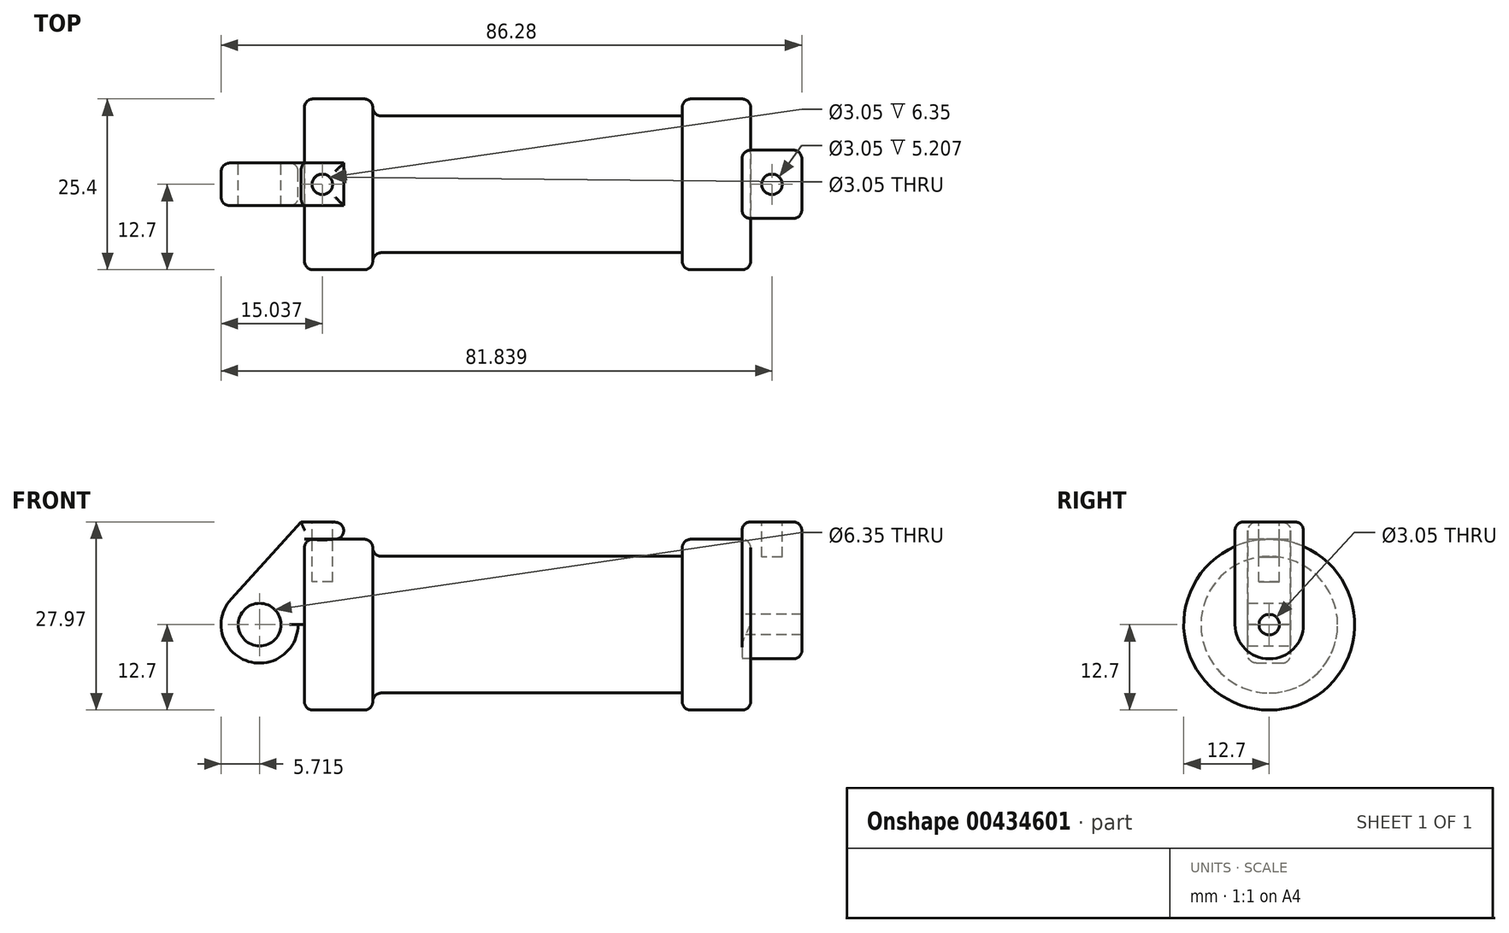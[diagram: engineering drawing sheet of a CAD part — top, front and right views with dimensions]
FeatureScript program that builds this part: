
annotation { "Feature Type Name" : "Feature", "Feature Type Description" : "" }
export const myFeature = defineFeature(function(context is Context, id is Id, definition is map)
    precondition{}
    {
        {
            var Q0;
            Q0=qCreatedBy(makeId("Front.planeOp"),FACE);
            var sketch = newSketch(context, id + "F0", { "sketchPlane" : qUnion([Q0])});
            skLineSegment(sketch, "E0", {"start": v(0, 0) * mm, "end": v(0, 12.7) * mm});
            skLineSegment(sketch, "E1", {"start": v(0, 12.7) * mm, "end": v(10.16, 12.7) * mm});
            skLineSegment(sketch, "E2", {"start": v(10.16, 12.7) * mm, "end": v(10.16, 10.16) * mm});
            skLineSegment(sketch, "E3", {"start": v(10.16, 10.16) * mm, "end": v(56.13, 10.16) * mm});
            skLineSegment(sketch, "E4", {"start": v(56.13, 10.16) * mm, "end": v(56.13, 12.7) * mm});
            skLineSegment(sketch, "E5", {"start": v(56.13, 12.7) * mm, "end": v(66.3, 12.7) * mm});
            skLineSegment(sketch, "E6", {"start": v(66.3, 12.7) * mm, "end": v(66.3, 0) * mm});
            skLineSegment(sketch, "E7", {"start": v(66.3, 0) * mm, "end": v(0, 0) * mm});
            skLineSegment(sketch, "E8", {"start": v(5.84, 15.24) * mm, "end": v(-0.5, 15.24) * mm});
            skLineSegment(sketch, "E9", {"start": v(-0.5, 15.24) * mm, "end": v(-10.88, 3.85) * mm});
            skLineSegment(sketch, "E10", {"start": v(0, 0) * mm, "end": v(-6.65, 0) * mm});
            skCircle(sketch, "E11", {"center": v(-6.65, 0) * mm, "radius": 5.72 * mm});
            skCircle(sketch, "E12", {"center": v(-6.65, 0) * mm, "radius": 3.18 * mm});
            skLineSegment(sketch, "E13", {"start": v(5.84, 15.24) * mm, "end": v(5.84, -9.4) * mm});
            skLineSegment(sketch, "E14", {"start": v(5.84, -9.4) * mm, "end": v(-8.18, -5.5) * mm});
            skSolve(sketch);
        }
        {
            var Q0;
            {var subQ1=sQuery(id+"F0.wireOp",EDGE,"E0");Q0=makeQuery(id+"F0.imprint","IMPRINT",FACE,{"disambiguationData":[TD([[makeQuery(id+"F0.imprint","IMPRINT",EDGE,{"derivedFrom":subQ1}),1.0]])]});}
            var Q1;
            {var subQ5=sQuery(id+"F0.wireOp",EDGE,"E12");Q1=makeQuery(id+"F0.imprint","IMPRINT",FACE,{"disambiguationData":[TD([[makeQuery(id+"F0.imprint","IMPRINT",EDGE,{"derivedFrom":subQ5}),-1.0]])]});}
            extrude(context, id + "F1", {"entities" : qUnion([Q0, Q1]), "endBound" : BoundingType.SYMMETRIC, "depth" : 6.35 * mm});
        }
        {
            var Q0;
            {var subQ0=sQuery(id+"F0.wireOp",EDGE,"E0");Q0=makeQuery(id+"F0.imprint","IMPRINT",FACE,{"disambiguationData":[TD([[makeQuery(id+"F0.imprint","IMPRINT",EDGE,{"derivedFrom":subQ0}),-1.0]])]});}
            var Q1;
            {var subQ0=sQuery(id+"F0.wireOp",EDGE,"E2");Q1=makeQuery(id+"F0.imprint","IMPRINT",FACE,{"disambiguationData":[TD([[makeQuery(id+"F0.imprint","IMPRINT",EDGE,{"derivedFrom":subQ0}),-1.0]])]});}
            var Q2;
            Q2=sQuery(id+"F0.wireOp",EDGE,"E7");
            revolve(context, id + "F2", {"entities" : qUnion([Q0, Q1]), "axis" : qUnion([Q2]), "revolveType" : RevolveType.FULL});
        }
        {
            var Q0;
            Q0=makeQuery(id+"F2.opRevolve","SWEPT_FACE",FACE,{"disambiguationData":[OSD([sQuery(id+"F0.wireOp",EDGE,"E6")])]});
            var sketch = newSketch(context, id + "F3", { "sketchPlane" : qUnion([Q0])});
            skCircle(sketch, "E15", {"center": v(0, 0) * mm, "radius": 1.52 * mm});
            skCircle(sketch, "E16", {"center": v(0, 0) * mm, "radius": 5.08 * mm});
            skLineSegment(sketch, "E17", {"start": v(-5.08, 0) * mm, "end": v(-5.08, 15.27) * mm});
            skLineSegment(sketch, "E18", {"start": v(5.08, 0) * mm, "end": v(5.08, 15.27) * mm});
            skLineSegment(sketch, "E19", {"start": v(5.08, 15.27) * mm, "end": v(-5.08, 15.27) * mm});
            skSolve(sketch);
        }
        {
            var Q0;
            {var subQ0=sQuery(id+"F3.wireOp",EDGE,"E17");var subQ1=sQuery(id+"F3.wireOp",EDGE,"E16");var subQ2=makeQuery(id+"F3.imprint","INTERSECT",VERTEX,{"derivedFrom":[subQ1,subQ0]});Q0=makeQuery(id+"F3.imprint","IMPRINT",FACE,{"disambiguationData":[TD([[makeQuery(id+"F3.imprint","IMPRINT",EDGE,{"disambiguationData":[TD([[subQ2,1.0]])],"derivedFrom":subQ1}),-1.0]])]});}
            var Q1;
            {var subQ0=sQuery(id+"F3.wireOp",EDGE,"E19");Q1=makeQuery(id+"F3.imprint","IMPRINT",FACE,{"disambiguationData":[TD([[makeQuery(id+"F3.imprint","IMPRINT",EDGE,{"derivedFrom":subQ0}),1.0]])]});}
            var Q2;
            Q2=makeQuery(id+"F3.imprint","IMPRINT",FACE,{"disambiguationData":[TD([[makeQuery(id+"F3.imprint","IMPRINT",EDGE,{"derivedFrom":sQuery(id+"F3.wireOp",EDGE,"E15")}),-1.0]])]});
            extrude(context, id + "F4", {"entities" : qUnion([Q0, Q1, Q2]), "depth" : 7.62 * mm, "hasSecondDirection" : true, "secondDirectionOppositeDirection" : true, "secondDirectionDepth" : 1.27 * mm});
        }
        {
            var Q0;
            Q0=makeQuery(id+"F4.opExtrude","SWEPT_FACE",FACE,{"disambiguationData":[OSD([sQuery(id+"F3.wireOp",EDGE,"E19")])]});
            var sketch = newSketch(context, id + "F5", { "sketchPlane" : qUnion([Q0])});
            skCircle(sketch, "E20", {"center": v(69.47, 0) * mm, "radius": 1.52 * mm});
            skPoint(sketch, "E21.orphan", {"position": v(69.47, 5.08) * mm});
            skPoint(sketch, "E22.orphan", {"position": v(73.91, 0) * mm});
            skPoint(sketch, "E23.orphan", {"position": v(69.47, -5.08) * mm});
            skPoint(sketch, "E24.start.orphan", {"position": v(65.02, 0) * mm});
            skSolve(sketch);
        }
        {
            var Q0;
            Q0=makeQuery(id+"F5.imprint","IMPRINT",FACE,{"disambiguationData":[TD([[makeQuery(id+"F5.imprint","IMPRINT",EDGE,{"derivedFrom":sQuery(id+"F5.wireOp",EDGE,"E20")}),1.0]])]});
            extrude(context, id + "F6", {"entities" : qUnion([Q0]), "operationType" : NewBodyOperationType.REMOVE, "endBound" : BoundingType.SYMMETRIC, "oppositeDirection" : true, "depth" : 10.4 * mm});
        }
        {
            var Q0;
            Q0=makeQuery(id+"F1.opExtrude","SWEPT_FACE",FACE,{"disambiguationData":[OSD([sQuery(id+"F0.wireOp",EDGE,"E8")])]});
            var sketch = newSketch(context, id + "F7", { "sketchPlane" : qUnion([Q0])});
            skCircle(sketch, "E25", {"center": v(2.67, 0) * mm, "radius": 1.52 * mm});
            skPoint(sketch, "E26.trimOffspring.end.orphan", {"position": v(5.84, 0) * mm});
            skPoint(sketch, "E27.trimOffspring.end.orphan", {"position": v(2.67, -3.18) * mm});
            skPoint(sketch, "E28.start.orphan", {"position": v(-0.5, 0) * mm});
            skPoint(sketch, "E29.start.orphan", {"position": v(2.67, 3.18) * mm});
            skSolve(sketch);
        }
        {
            var Q0;
            Q0 = qSketchRegion(id + "F7", true);
            extrude(context, id + "F8", {"entities" : qUnion([Q0]), "operationType" : NewBodyOperationType.REMOVE, "endBound" : BoundingType.SYMMETRIC, "oppositeDirection" : true, "depth" : 17.78 * mm});
        }
        {
            var Q0;
            Q0=makeQuery(id+"F1.opExtrude","CAP_EDGE",EDGE,{"disambiguationData":[OSD([sQuery(id+"F0.wireOp",EDGE,"E8")])],"isStart":true});
            var Q1;
            Q1=makeQuery(id+"F1.opExtrude","SWEPT_EDGE",EDGE,{"disambiguationData":[OSD([sQuery(id+"F0.wireOp",EDGE,"E8"),sQuery(id+"F0.wireOp",EDGE,"E13")])]});
            var Q2;
            Q2=makeQuery(id+"F1.opExtrude","CAP_EDGE",EDGE,{"disambiguationData":[OSD([sQuery(id+"F0.wireOp",EDGE,"E8")])],"isStart":false});
            var Q3;
            Q3=makeQuery(id+"F1.opExtrude","CAP_EDGE",EDGE,{"disambiguationData":[OSD([sQuery(id+"F0.wireOp",EDGE,"E9")])],"isStart":false});
            var Q4;
            Q4=makeQuery(id+"F1.opExtrude","CAP_EDGE",EDGE,{"disambiguationData":[OSD([sQuery(id+"F0.wireOp",EDGE,"E11")])],"isStart":false});
            var Q5;
            Q5=makeQuery(id+"F1.opExtrude","SWEPT_EDGE",EDGE,{"disambiguationData":[OSD([sQuery(id+"F0.wireOp",EDGE,"E1"),sQuery(id+"F0.wireOp",EDGE,"E13")])]});
            var Q6;
            Q6=makeQuery(id+"F1.opExtrude","CAP_EDGE",EDGE,{"disambiguationData":[OSD([sQuery(id+"F0.wireOp",EDGE,"E9")])],"isStart":true});
            var Q7;
            Q7=makeQuery(id+"F1.opExtrude","CAP_EDGE",EDGE,{"disambiguationData":[OSD([sQuery(id+"F0.wireOp",EDGE,"E11")])],"isStart":true});
            var Q8;
            Q8=makeQuery(id+"F4.opExtrude","CAP_EDGE",EDGE,{"disambiguationData":[OSD([sQuery(id+"F3.wireOp",EDGE,"E19")])],"isStart":false});
            var Q9;
            Q9=makeQuery(id+"F4.opExtrude","SWEPT_EDGE",EDGE,{"disambiguationData":[OSD([sQuery(id+"F3.wireOp",EDGE,"E17"),sQuery(id+"F3.wireOp",EDGE,"E19")])]});
            var Q10;
            Q10=makeQuery(id+"F4.opExtrude","SWEPT_EDGE",EDGE,{"disambiguationData":[OSD([sQuery(id+"F3.wireOp",EDGE,"E18"),sQuery(id+"F3.wireOp",EDGE,"E19")])]});
            var Q11;
            Q11=makeQuery(id+"F4.opExtrude","CAP_EDGE",EDGE,{"disambiguationData":[OSD([sQuery(id+"F3.wireOp",EDGE,"E19")])],"isStart":true});
            var Q12;
            Q12=makeQuery(id+"F4.opExtrude","CAP_EDGE",EDGE,{"disambiguationData":[OSD([sQuery(id+"F3.wireOp",EDGE,"E17")])],"isStart":false});
            var Q13;
            Q13=makeQuery(id+"F4.opExtrude","CAP_EDGE",EDGE,{"disambiguationData":[OSD([sQuery(id+"F3.wireOp",EDGE,"E18")])],"isStart":false});
            var Q14;
            Q14=makeQuery(id+"F4.opExtrude","CAP_EDGE",EDGE,{"disambiguationData":[OSD([sQuery(id+"F3.wireOp",EDGE,"E16")])],"isStart":false});
            var Q15;
            Q15=makeQuery(id+"F2.opRevolve","SWEPT_EDGE",EDGE,{"disambiguationData":[OSD([sQuery(id+"F0.wireOp",EDGE,"E5"),sQuery(id+"F0.wireOp",EDGE,"E6")])]});
            var Q16;
            Q16=makeQuery(id+"F2.opRevolve","SWEPT_EDGE",EDGE,{"disambiguationData":[OSD([sQuery(id+"F0.wireOp",EDGE,"E4"),sQuery(id+"F0.wireOp",EDGE,"E5")])]});
            var Q17;
            Q17=makeQuery(id+"F2.opRevolve","SWEPT_EDGE",EDGE,{"disambiguationData":[OSD([sQuery(id+"F0.wireOp",EDGE,"E1"),sQuery(id+"F0.wireOp",EDGE,"E2")])]});
            var Q18;
            Q18=makeQuery(id+"F2.opRevolve","SWEPT_EDGE",EDGE,{"disambiguationData":[OSD([sQuery(id+"F0.wireOp",EDGE,"E2"),sQuery(id+"F0.wireOp",EDGE,"E3")])]});
            var Q19;
            Q19=makeQuery(id+"F2.opRevolve","SWEPT_EDGE",EDGE,{"disambiguationData":[OSD([sQuery(id+"F0.wireOp",EDGE,"E0"),sQuery(id+"F0.wireOp",EDGE,"E1")])]});
            var Q20;
            Q20=makeQuery(id+"F4.opExtrude","CAP_EDGE",EDGE,{"disambiguationData":[OSD([sQuery(id+"F3.wireOp",EDGE,"E18")])],"isStart":true});
            var Q21;
            Q21=makeQuery(id+"F4.opExtrude","CAP_EDGE",EDGE,{"disambiguationData":[OSD([sQuery(id+"F3.wireOp",EDGE,"E17")])],"isStart":true});
            fillet(context, id + "F9", {"entities" : qUnion([Q0, Q1, Q2, Q3, Q4, Q5, Q6, Q7, Q8, Q9, Q10, Q11, Q12, Q13, Q14, Q15, Q16, Q17, Q18, Q19, Q20, Q21]), "radius" : 1.27 * mm, "allowEdgeOverflow" : false});
        }
    });
